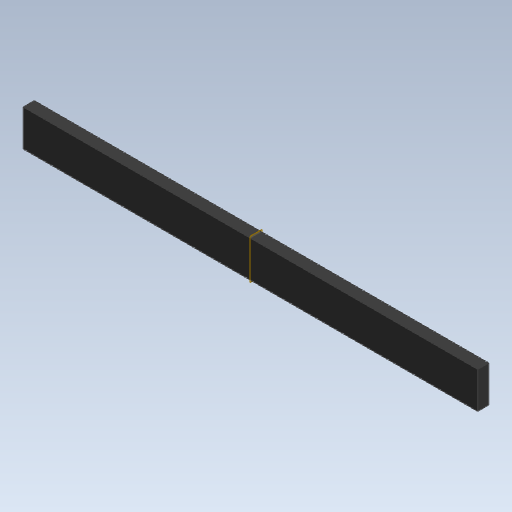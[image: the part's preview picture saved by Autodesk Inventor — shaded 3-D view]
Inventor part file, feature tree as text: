
AUTODESK INVENTOR PART (.ipt)
format: ipt  version: 2020 (Build 240168000, 168)  size: 98,304 bytes
history: native  units: mm
features: other x1, extrude x1
ambient origin geometry x8: Origin, YZ Plane, XZ Plane, XY Plane, X Axis, Y Axis, Z Axis, Center Point
bodies: Body1 (feature_tree)
feature tree (2):
  other  "實體1"
  extrude  "擠出1"  Depth=10.0mm
